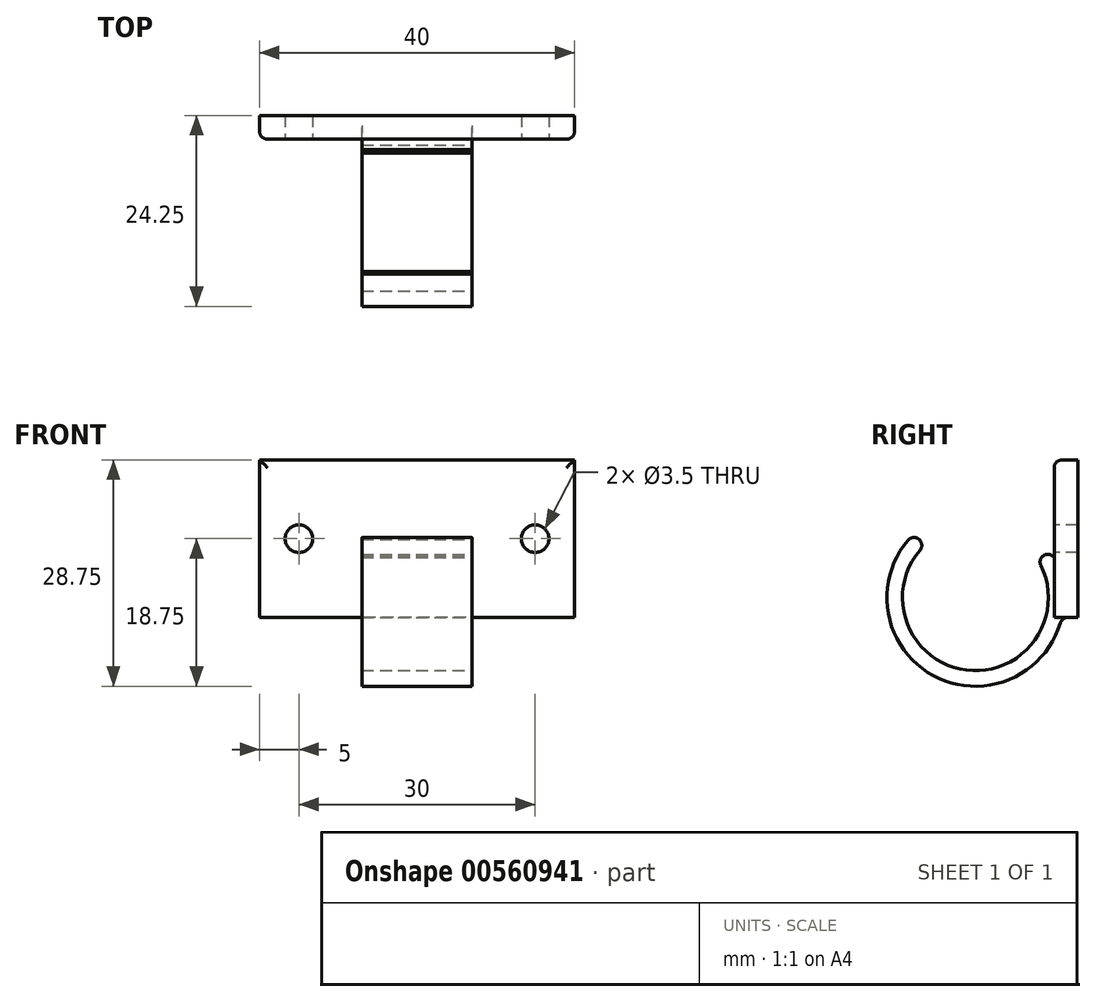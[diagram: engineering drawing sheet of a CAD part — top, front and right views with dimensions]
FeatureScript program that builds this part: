
annotation { "Feature Type Name" : "Feature", "Feature Type Description" : "" }
export const myFeature = defineFeature(function(context is Context, id is Id, definition is map)
    precondition{}
    {
        {
            var Q0;
            Q0=qCreatedBy(makeId("Top.planeOp"),FACE);
            var sketch = newSketch(context, id + "F0", { "sketchPlane" : qUnion([Q0])});
            skLineSegment(sketch, "E0.bottom", {"start": v(0, 0) * mm, "end": v(20, 0) * mm});
            skLineSegment(sketch, "E0.top", {"start": v(0, -3) * mm, "end": v(20.5, -3) * mm});
            skLineSegment(sketch, "E1.bottom", {"start": v(0, -3) * mm, "end": v(-2.5, -3) * mm});
            skLineSegment(sketch, "E2", {"start": v(20.5, -3) * mm, "end": v(23.5, -3) * mm});
            skLineSegment(sketch, "E3", {"start": v(0, 0) * mm, "end": v(-10, 0) * mm});
            skLineSegment(sketch, "E4", {"start": v(-10, 0) * mm, "end": v(-10, -3) * mm});
            skLineSegment(sketch, "E5", {"start": v(-10, -3) * mm, "end": v(-2.5, -3) * mm});
            skLineSegment(sketch, "E6", {"start": v(20, 0) * mm, "end": v(30, 0) * mm});
            skLineSegment(sketch, "E7", {"start": v(30, 0) * mm, "end": v(30, -3) * mm});
            skLineSegment(sketch, "E8", {"start": v(30, -3) * mm, "end": v(23.5, -3) * mm});
            skSolve(sketch);
        }
        {
            var Q0;
            Q0=makeQuery(id+"F0.imprint","IMPRINT",FACE,{"disambiguationData":[TD([[makeQuery(id+"F0.imprint","IMPRINT",EDGE,{"derivedFrom":sQuery(id+"F0.wireOp",EDGE,"E0.bottom")}),-1.0]])]});
            extrude(context, id + "F1", {"entities" : qUnion([Q0]), "depth" : 5 * mm, "offsetDistance" : 25 * mm});
        }
        {
            var Q0;
            Q0=qCreatedBy(makeId("Front.planeOp"),FACE);
            cPlane(context, id + "F2", {"entities" : qUnion([Q0]), "cplaneType" : CPlaneType.OFFSET, "offset" : 3 * mm, "width" : 150 * mm, "height" : 150 * mm});
        }
        {
            var Q0;
            Q0=qCreatedBy(makeId("Right.planeOp"),FACE);
            cPlane(context, id + "F3", {"entities" : qUnion([Q0]), "cplaneType" : CPlaneType.OFFSET, "offset" : 10 * mm, "width" : 150 * mm, "height" : 150 * mm});
        }
        {
            var Q0;
            Q0=qCreatedBy(id+"F3.planeOp",FACE);
            var sketch = newSketch(context, id + "F4", { "sketchPlane" : qUnion([Q0])});
            skLineSegment(sketch, "E9", {"start": v(0, 0) * mm, "end": v(0, 9.78) * mm, "construction": true});
            skLineSegment(sketch, "E10.0", {"start": v(-3, 0) * mm, "end": v(-3, 9.78) * mm, "construction": true});
            skLineSegment(sketch, "E11", {"start": v(-3, 3.2) * mm, "end": v(-3, 0) * mm});
            skLineSegment(sketch, "E12", {"start": v(-3, 0) * mm, "end": v(-3, 2.5) * mm, "construction": true});
            skLineSegment(sketch, "E13", {"start": v(-3.75, 2.5) * mm, "end": v(-13, 2.5) * mm, "construction": true});
            skLineSegment(sketch, "E14", {"start": v(-6.28, 7.33) * mm, "end": v(-19.74, 9.02) * mm, "construction": true});
            skPoint(sketch, "E15.visualSharp", {"position": v(-3.32, 0) * mm});
            skLineSegment(sketch, "E16", {"start": v(-2.94, 5) * mm, "end": v(-2.94, 5) * mm});
            skPoint(sketch, "E17.visualSharp", {"position": v(-3.32, 5) * mm});
            skArc(sketch, "E18", {"start": v(-21.56, 9.8) * mm, "mid": v(-18.37, -7.39) * mm, "end": v(-2.22, -0.71) * mm});
            skLineSegment(sketch, "E19", {"start": v(-2.03, 5) * mm, "end": v(-2.03, 0) * mm});
            skArc(sketch, "E20.trimOffspring", {"start": v(-2.22, 5.71) * mm, "mid": v(-2.52, 6.6) * mm, "end": v(-2.9, 7.46) * mm});
            skLineSegment(sketch, "E21", {"start": v(-1.26, 5) * mm, "end": v(0, 5) * mm});
            skLineSegment(sketch, "E22", {"start": v(0, 5) * mm, "end": v(0, 0) * mm});
            skPoint(sketch, "E23.visualSharp", {"position": v(-2.03, 5) * mm});
            skArc(sketch, "E23.filletArc", {"start": v(-2.22, 5.71) * mm, "mid": v(-1.86, 5.2) * mm, "end": v(-1.26, 5) * mm});
            skLineSegment(sketch, "E24", {"start": v(0, 0) * mm, "end": v(-1.26, 0) * mm});
            skPoint(sketch, "E25.visualSharp", {"position": v(-2.03, 0) * mm});
            skArc(sketch, "E25.filletArc", {"start": v(-1.26, 0) * mm, "mid": v(-1.86, -0.2) * mm, "end": v(-2.22, -0.71) * mm});
            skPoint(sketch, "E26.visualSharp", {"position": v(-3.43, 8.42) * mm});
            skArc(sketch, "E26.filletArc", {"start": v(-2.9, 7.46) * mm, "mid": v(-3.52, 7.98) * mm, "end": v(-4.32, 7.87) * mm});
            skPoint(sketch, "E27.visualSharp", {"position": v(-20.87, 10.54) * mm});
            skArc(sketch, "E27.filletArc", {"start": v(-20.14, 9.9) * mm, "mid": v(-20.87, 10.15) * mm, "end": v(-21.56, 9.8) * mm});
            skArc(sketch, "E28", {"start": v(-20.06, 8.51) * mm, "mid": v(-14.15, -6.7) * mm, "end": v(-4.68, 6.6) * mm});
            skLineSegment(sketch, "E29", {"start": v(-20.15, 9.9) * mm, "end": v(-20.14, 9.9) * mm});
            skLineSegment(sketch, "E30", {"start": v(-4.3, 7.89) * mm, "end": v(-4.32, 7.87) * mm});
            skPoint(sketch, "E31.visualSharp", {"position": v(-19.38, 9.22) * mm});
            skArc(sketch, "E31.filletArc", {"start": v(-20.06, 8.51) * mm, "mid": v(-19.82, 9.23) * mm, "end": v(-20.15, 9.9) * mm});
            skPoint(sketch, "E32.visualSharp", {"position": v(-5.12, 7.39) * mm});
            skArc(sketch, "E32.filletArc", {"start": v(-4.3, 7.89) * mm, "mid": v(-4.74, 7.31) * mm, "end": v(-4.68, 6.6) * mm});
            skSolve(sketch);
        }
        {
            var Q0;
            {var subQ1=sQuery(id+"F4.wireOp",EDGE,"E18");Q0=makeQuery(id+"F4.imprint","IMPRINT",FACE,{"disambiguationData":[TD([[makeQuery(id+"F4.imprint","IMPRINT",EDGE,{"derivedFrom":subQ1}),1.0]])]});}
            extrude(context, id + "F5", {"entities" : qUnion([Q0]), "operationType" : NewBodyOperationType.ADD, "oppositeDirection" : true, "depth" : 7 * mm, "offsetDistance" : 25 * mm});
        }
        {
            var Q0;
            {var subQ1=sQuery(id+"F4.wireOp",EDGE,"E18");Q0=makeQuery(id+"F4.imprint","IMPRINT",FACE,{"disambiguationData":[TD([[makeQuery(id+"F4.imprint","IMPRINT",EDGE,{"derivedFrom":subQ1}),1.0]])]});}
            extrude(context, id + "F6", {"entities" : qUnion([Q0]), "operationType" : NewBodyOperationType.ADD, "depth" : 7 * mm, "offsetDistance" : 25 * mm});
        }
        {
            var Q0;
            Q0=makeQuery(id+"F0.imprint","IMPRINT",FACE,{"disambiguationData":[TD([[makeQuery(id+"F0.imprint","IMPRINT",EDGE,{"derivedFrom":sQuery(id+"F0.wireOp",EDGE,"E0.bottom")}),-1.0]])]});
            extrude(context, id + "F7", {"entities" : qUnion([Q0]), "operationType" : NewBodyOperationType.ADD, "depth" : 20 * mm, "offsetDistance" : 25 * mm});
        }
        {
            var Q0;
            {var subQ0=sQuery(id+"F0.wireOp",EDGE,"E8");var subQ1=sQuery(id+"F0.wireOp",EDGE,"E5");var subQ2=sQuery(id+"F0.wireOp",EDGE,"E2");var subQ3=sQuery(id+"F0.wireOp",EDGE,"E1.bottom");var subQ4=sQuery(id+"F0.wireOp",EDGE,"E0.top");var subQ5=sQuery(id+"F0.wireOp",EDGE,"E7");var subQ7=sQuery(id+"F0.wireOp",EDGE,"E4");var subQ24=makeQuery(id+"F1.opExtrude","SWEPT_FACE",FACE,{"disambiguationData":[OSD([subQ4,subQ3,subQ2,subQ1,subQ0])]});Q0=makeQuery(id+"F7.boolean.opBoolean","MERGE",FACE,{"derivedFrom":[makeQuery(id+"F5.boolean.opBoolean","SPLIT",FACE,{"disambiguationData":[TD([makeQuery(id+"F1.opExtrude","SWEPT_FACE",FACE,{"disambiguationData":[OSD([subQ7])]})])],"derivedFrom":subQ24}),makeQuery(id+"F5.boolean.opBoolean","SPLIT",FACE,{"disambiguationData":[TD([makeQuery(id+"F1.opExtrude","SWEPT_FACE",FACE,{"disambiguationData":[OSD([subQ5])]})])],"derivedFrom":subQ24}),makeQuery(id+"F7.opExtrude","SWEPT_FACE",FACE,{"disambiguationData":[OSD([subQ4,subQ3,subQ2,subQ1,subQ0])]})]});}
            var sketch = newSketch(context, id + "F8", { "sketchPlane" : qUnion([Q0])});
            skLineSegment(sketch, "E33.0", {"start": v(-5, 20) * mm, "end": v(-5, 0) * mm, "construction": true});
            skLineSegment(sketch, "E34.0", {"start": v(25, 20) * mm, "end": v(25, 0) * mm, "construction": true});
            skLineSegment(sketch, "E35.0", {"start": v(30, 10) * mm, "end": v(-10, 10) * mm, "construction": true});
            skCircle(sketch, "E36", {"center": v(-5, 10) * mm, "radius": 1.75 * mm});
            skCircle(sketch, "E37", {"center": v(25, 10) * mm, "radius": 1.75 * mm});
            skSolve(sketch);
        }
        {
            var Q0;
            Q0=makeQuery(id+"F8.imprint","IMPRINT",FACE,{"disambiguationData":[TD([[makeQuery(id+"F8.imprint","IMPRINT",EDGE,{"derivedFrom":sQuery(id+"F8.wireOp",EDGE,"E36")}),1.0]])]});
            var Q1;
            Q1=makeQuery(id+"F8.imprint","IMPRINT",FACE,{"disambiguationData":[TD([[makeQuery(id+"F8.imprint","IMPRINT",EDGE,{"derivedFrom":sQuery(id+"F8.wireOp",EDGE,"E37")}),1.0]])]});
            extrude(context, id + "F9", {"entities" : qUnion([Q0, Q1]), "operationType" : NewBodyOperationType.REMOVE, "oppositeDirection" : true, "depth" : 25 * mm, "offsetDistance" : 25 * mm});
        }
        {
            var Q0;
            Q0=makeQuery(id+"F7.opExtrude","CAP_EDGE",EDGE,{"disambiguationData":[OSD([sQuery(id+"F0.wireOp",EDGE,"E0.top"),sQuery(id+"F0.wireOp",EDGE,"E1.bottom"),sQuery(id+"F0.wireOp",EDGE,"E2"),sQuery(id+"F0.wireOp",EDGE,"E5"),sQuery(id+"F0.wireOp",EDGE,"E8")])],"isStart":false});
            var Q1;
            {var subQ0=sQuery(id+"F0.wireOp",EDGE,"E8");var subQ1=sQuery(id+"F0.wireOp",EDGE,"E7");Q1=makeQuery(id+"F7.boolean.opBoolean","MERGE",EDGE,{"derivedFrom":[makeQuery(id+"F1.opExtrude","SWEPT_EDGE",EDGE,{"disambiguationData":[OSD([subQ1,subQ0])]}),makeQuery(id+"F7.opExtrude","SWEPT_EDGE",EDGE,{"disambiguationData":[OSD([subQ1,subQ0])]})]});}
            var Q2;
            {var subQ0=sQuery(id+"F0.wireOp",EDGE,"E5");var subQ1=sQuery(id+"F0.wireOp",EDGE,"E4");Q2=makeQuery(id+"F7.boolean.opBoolean","MERGE",EDGE,{"derivedFrom":[makeQuery(id+"F1.opExtrude","SWEPT_EDGE",EDGE,{"disambiguationData":[OSD([subQ1,subQ0])]}),makeQuery(id+"F7.opExtrude","SWEPT_EDGE",EDGE,{"disambiguationData":[OSD([subQ1,subQ0])]})]});}
            var Q3;
            Q3=makeQuery(id+"F9.boolean.opBoolean","COPY",EDGE,{"derivedFrom":makeQuery(id+"F9.opExtrude","CAP_EDGE",EDGE,{"disambiguationData":[OSD([sQuery(id+"F8.wireOp",EDGE,"E36")])],"isStart":true})});
            var Q4;
            Q4=makeQuery(id+"F9.boolean.opBoolean","COPY",EDGE,{"derivedFrom":makeQuery(id+"F9.opExtrude","CAP_EDGE",EDGE,{"disambiguationData":[OSD([sQuery(id+"F8.wireOp",EDGE,"E37")])],"isStart":true})});
            fillet(context, id + "F10", {"entities" : qUnion([Q0, Q1, Q2, Q3, Q4]), "radius" : 1 * mm, "tangentPropagation" : true, "allowEdgeOverflow" : false});
        }
    });
